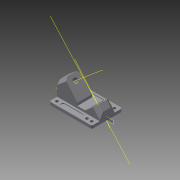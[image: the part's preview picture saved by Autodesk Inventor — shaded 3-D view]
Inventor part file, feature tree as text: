
AUTODESK INVENTOR PART (.ipt)
format: ipt  version: 2015 (Build 190159000, 159)  size: 342,528 bytes
history: native  units: in
note: dims shown in document units (in); Inventor stores cm internally (conversion verified against a paired STEP export)
features: sketch x15, extrude x13, projected_geometry x9, plane x3, chamfer x3, other x3, mirror x1, draft x1, fillet x1
ambient origin geometry x8: Origin, YZ Plane, XZ Plane, XY Plane, X Axis, Y Axis, Z Axis, Center Point
bodies: Solid1 (feature_tree)
feature tree (49):
  extrude  "Extrusion1"  Depth=2.2in
  plane  "Work Plane1"
  extrude  "Extrusion2"  Depth=0.21in TaperAngle=0.0deg
  extrude  "Extrusion3"  Depth=0.205in
  mirror  "Mirror1"
  extrude  "Extrusion4"  Depth=0.278in
  extrude  "Extrusion5"  Depth=0.278in
  extrude  "Extrusion6"  Depth=0.278in
  chamfer  "Chamfer1"  Distance=0.21in
  extrude  "Extrusion7"  Depth=0.3in
  chamfer  "Chamfer2"  Distance=0.05in
  other  "Work Axis1"
  extrude  "Extrusion8"  Depth=0.57in
  extrude  "Extrusion9"  Depth=1.06in
  chamfer  "Chamfer3"  Distance=0.65in
  extrude  "Extrusion10"  Depth=0.3436in
  draft  "FaceDraft5"
  extrude  "Extrusion11"  Depth=0.25in TaperAngle=45.0deg
  sketch  "Sketch14"  dims[d24=0.15in d25=0.0in d26=1.06in d27=0.65in d28=0.0in]
  sketch  "Sketch15"  dims[d34=0.3436in d35=0.3436in]
  extrude  "Extrusion13"  Depth=0.5in
  fillet  "Fillet2"  Radius=0.5in
  other  "Work Axis2"
  extrude  "Extrusion14"  Depth=0.25in TaperAngle=45.0deg
  plane  "Work Plane4"
  sketch  "Sketch18"  dims[d41=0.7in d42=0.5in d43=0.5in d44=0.0in d46=0.25in d47=0.125in d48=45.0deg d49=1.46in d50=1.3in d51=0.0in d52=0.2in d53=0.3436in d54=0.3436in d55=1.3in d56=0.0in d57=0.2in d58=0.125in d59=45.0deg d63=0.66in d64=0.125in d65=0.4in d66=0.0in d67=0.3436in d68=0.37in d69=0.4in d70=0.0in d71=1.1in d72=0.76in d73=0.0in d74=0.11in d75=0.8in d76=0.8933in d77=90.0deg d78=0.4in d79=0.4in d82=0.76in d83=0.0in d84=0.135in d85=1.08in d86=0.75in d87=0.05in d88=0.05in d89=0.5in d90=0.03in d91=0.0in d92=0.0137in]
  other  "Work Axis3"
  sketch  "Sketch1"  dims[d0=3.074in d1=2.2in]
  sketch  "Sketch2"  dims[d2=0.1in d3=0.21in d4=0.0in]
  sketch  "Sketch3"  dims[d5=0.205in d6=0.205in]
  plane  "Work Plane2"
  sketch  "Sketch4"  dims[d7=0.205in d8=0.278in]
  projected_geometry  "Projected Loop1"
  sketch  "Sketch5"  dims[d9=0.278in d10=0.278in]
  projected_geometry  "Projected Loop2"
  sketch  "Sketch8"  dims[d11=0.278in d12=0.278in]
  projected_geometry  "Projected Loop4"
  sketch  "Sketch9"  dims[d13=0.35in d14=0.21in d15=0.0in]
  sketch  "Sketch10"  dims[d16=0.3in d17=0.45in]
  projected_geometry  "Projected Loop5"
  sketch  "Sketch11"  dims[d18=0.45in]
  projected_geometry  "Projected Loop6"
  sketch  "Sketch12"  dims[d19=0.0in d20=0.05in d21=0.0in]
  projected_geometry  "Projected Loop7"
  sketch  "Sketch13"  dims[d22=0.57in d23=0.57in]
  projected_geometry  "Projected Loop8"
  projected_geometry  "Projected Loop9"
  projected_geometry  "Projected Loop10"
  sketch  "Sketch17"  dims[d36=0.75in d37=0.0in d38=0.25in d39=0.125in d40=45.0deg]
